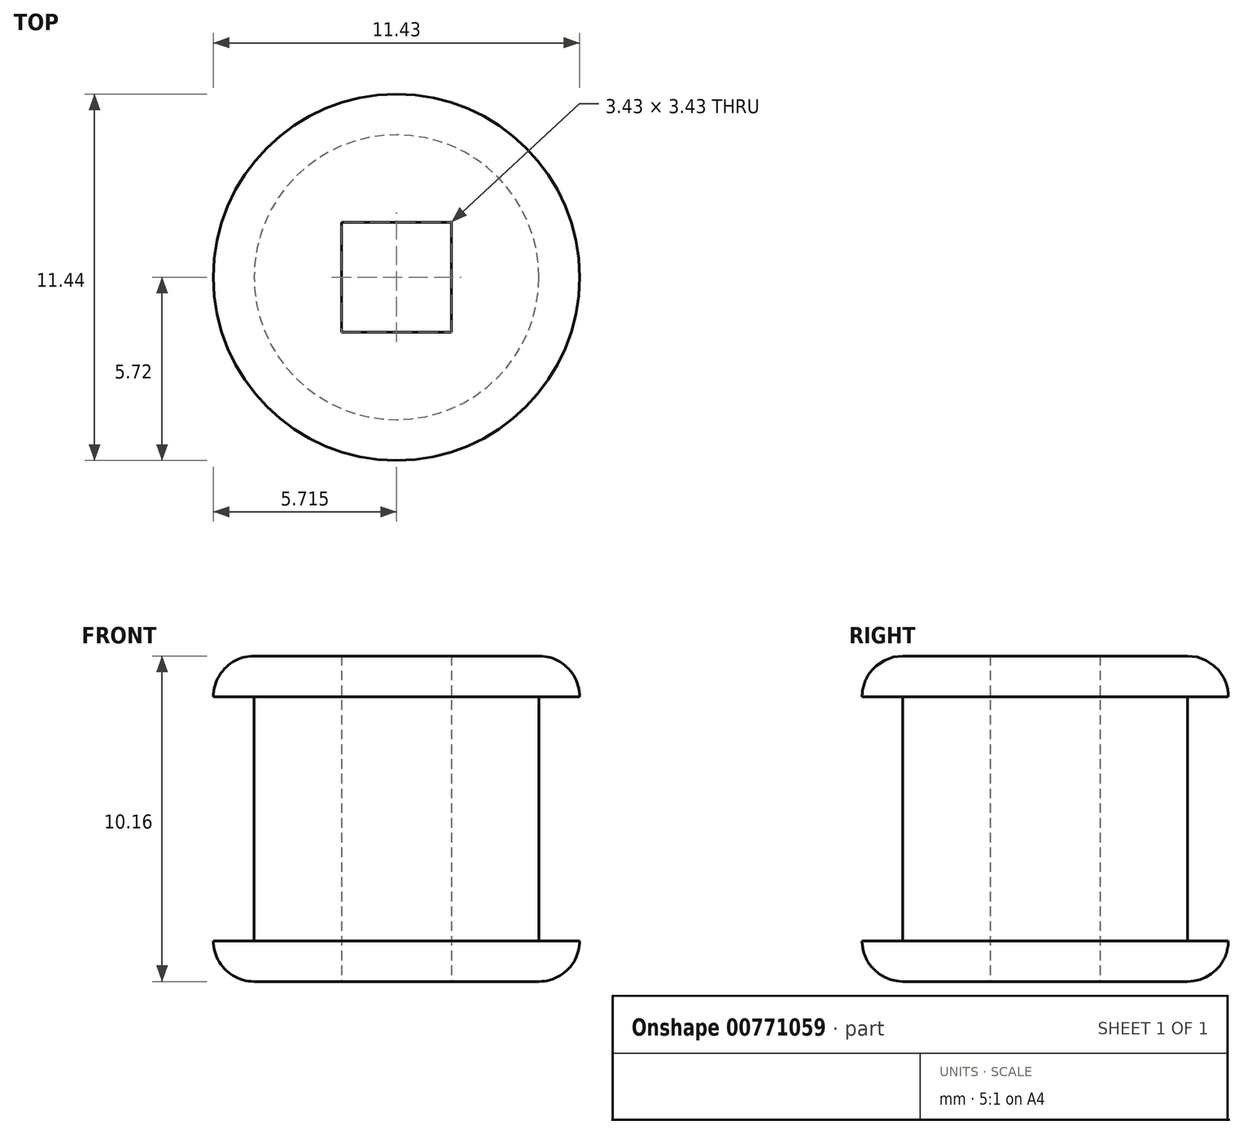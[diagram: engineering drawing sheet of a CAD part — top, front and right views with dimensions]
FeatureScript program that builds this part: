
annotation { "Feature Type Name" : "Feature", "Feature Type Description" : "" }
export const myFeature = defineFeature(function(context is Context, id is Id, definition is map)
    precondition{}
    {
        {
            var Q0;
            Q0=qCreatedBy(makeId("Front.planeOp"),FACE);
            var sketch = newSketch(context, id + "F0", { "sketchPlane" : qUnion([Q0])});
            skLineSegment(sketch, "E0", {"start": v(0, 0) * mm, "end": v(-1.27, 0) * mm});
            skLineSegment(sketch, "E1", {"start": v(-1.27, 0) * mm, "end": v(-1.27, 1.27) * mm});
            skLineSegment(sketch, "E2", {"start": v(-1.27, 1.27) * mm, "end": v(0, 1.27) * mm});
            skLineSegment(sketch, "E3", {"start": v(0, 1.27) * mm, "end": v(0, 8.9) * mm});
            skLineSegment(sketch, "E4", {"start": v(0, 8.9) * mm, "end": v(-1.27, 8.9) * mm});
            skLineSegment(sketch, "E5", {"start": v(-1.27, 8.9) * mm, "end": v(-1.27, 10.16) * mm});
            skLineSegment(sketch, "E6", {"start": v(-1.27, 10.16) * mm, "end": v(0, 10.16) * mm});
            skLineSegment(sketch, "E7", {"start": v(4.45, 0) * mm, "end": v(4.45, 13.24) * mm, "construction": true});
            skLineSegment(sketch, "E8", {"start": v(0, 10.16) * mm, "end": v(4.45, 10.16) * mm});
            skLineSegment(sketch, "E9", {"start": v(0, 0) * mm, "end": v(4.45, 0) * mm});
            skLineSegment(sketch, "E10", {"start": v(4.45, 10.16) * mm, "end": v(4.45, 0) * mm});
            skSolve(sketch);
        }
        {
            var Q0;
            Q0 = qSketchRegion(id + "F0", true);
            var Q1;
            Q1=sQuery(id+"F0.wireOp",EDGE,"E10");
            revolve(context, id + "F1", {"surfaceOperationType" : NewSurfaceOperationType.NEW, "entities" : qUnion([Q0]), "axis" : qUnion([Q1]), "revolveType" : RevolveType.FULL});
        }
        {
            var Q0;
            Q0=makeQuery(id+"F1.opRevolve","SWEPT_FACE",FACE,{"disambiguationData":[OSD([sQuery(id+"F0.wireOp",EDGE,"E0"),sQuery(id+"F0.wireOp",EDGE,"E9")])]});
            var sketch = newSketch(context, id + "F2", { "sketchPlane" : qUnion([Q0])});
            skCircle(sketch, "E11.0", {"center": v(4.45, 0) * mm, "radius": 4.44 * mm});
            skCircle(sketch, "E12.0", {"center": v(4.45, 0) * mm, "radius": 5.71 * mm});
            skLineSegment(sketch, "E13.bottom", {"start": v(6.16, -1.71) * mm, "end": v(2.73, -1.71) * mm});
            skLineSegment(sketch, "E13.top", {"start": v(6.16, 1.71) * mm, "end": v(2.73, 1.71) * mm});
            skLineSegment(sketch, "E13.left", {"start": v(6.16, -1.71) * mm, "end": v(6.16, 1.71) * mm});
            skLineSegment(sketch, "E13.right", {"start": v(2.73, -1.71) * mm, "end": v(2.73, 1.71) * mm});
            skSolve(sketch);
        }
        {
            var Q0;
            Q0=makeQuery(id+"F2.imprint","IMPRINT",FACE,{"disambiguationData":[TD([[makeQuery(id+"F2.imprint","IMPRINT",EDGE,{"derivedFrom":sQuery(id+"F2.wireOp",EDGE,"E13.bottom")}),-1.0]])]});
            extrude(context, id + "F3", {"entities" : qUnion([Q0]), "operationType" : NewBodyOperationType.REMOVE, "oppositeDirection" : true, "depth" : 25.4 * mm, "offsetDistance" : 25.4 * mm});
        }
        {
            var Q0;
            Q0=makeQuery(id+"F1.opRevolve","SWEPT_EDGE",EDGE,{"disambiguationData":[OSD([sQuery(id+"F0.wireOp",EDGE,"E0"),sQuery(id+"F0.wireOp",EDGE,"E1")])]});
            fillet(context, id + "F4", {"entities" : qUnion([Q0]), "radius" : 1.27 * mm, "tangentPropagation" : true, "allowEdgeOverflow" : false});
        }
        {
            var Q0;
            Q0=makeQuery(id+"F1.opRevolve","SWEPT_EDGE",EDGE,{"disambiguationData":[OSD([sQuery(id+"F0.wireOp",EDGE,"E5"),sQuery(id+"F0.wireOp",EDGE,"E6")])]});
            fillet(context, id + "F5", {"entities" : qUnion([Q0]), "radius" : 1.27 * mm, "tangentPropagation" : true, "allowEdgeOverflow" : false});
        }
    });
